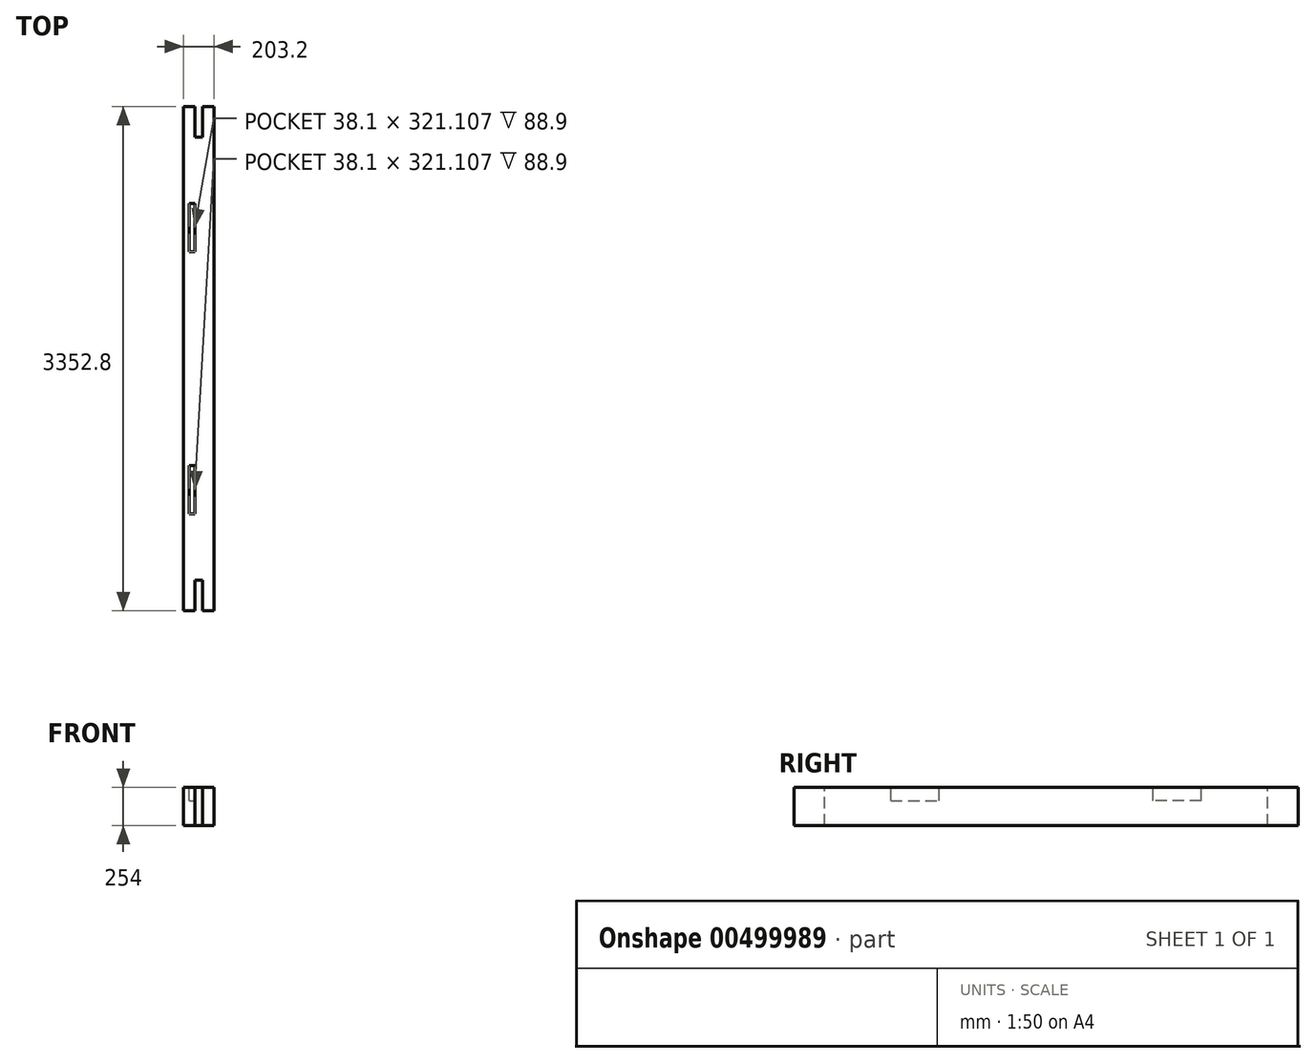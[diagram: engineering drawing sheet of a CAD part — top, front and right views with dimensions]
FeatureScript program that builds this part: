
annotation { "Feature Type Name" : "Feature", "Feature Type Description" : "" }
export const myFeature = defineFeature(function(context is Context, id is Id, definition is map)
    precondition{}
    {
        {
            var Q0;
            Q0=qCreatedBy(makeId("Top.planeOp"),FACE);
            var sketch = newSketch(context, id + "F0", { "sketchPlane" : qUnion([Q0])});
            skLineSegment(sketch, "E0.bottom", {"start": v(-101.6, 1676.4) * mm, "end": v(101.6, 1676.4) * mm});
            skLineSegment(sketch, "E0.top", {"start": v(-101.6, -1676.4) * mm, "end": v(101.6, -1676.4) * mm});
            skLineSegment(sketch, "E0.left", {"start": v(-101.6, 1676.4) * mm, "end": v(-101.6, -1676.4) * mm});
            skLineSegment(sketch, "E0.right", {"start": v(101.6, 1676.4) * mm, "end": v(101.6, -1676.4) * mm});
            skPoint(sketch, "E0.middle", {"position": v(0, 0) * mm});
            skLineSegment(sketch, "E1.bottom", {"start": v(-25.4, -1676.4) * mm, "end": v(25.4, -1676.4) * mm});
            skLineSegment(sketch, "E1.top", {"start": v(-25.4, -1473.2) * mm, "end": v(25.4, -1473.2) * mm});
            skLineSegment(sketch, "E1.left", {"start": v(-25.4, -1676.4) * mm, "end": v(-25.4, -1473.2) * mm});
            skLineSegment(sketch, "E1.right", {"start": v(25.4, -1676.4) * mm, "end": v(25.4, -1473.2) * mm});
            skLineSegment(sketch, "E2.bottom", {"start": v(-63.5, -1032.3) * mm, "end": v(-25.4, -1032.3) * mm});
            skLineSegment(sketch, "E2.top", {"start": v(-63.5, -711.2) * mm, "end": v(-25.4, -711.2) * mm});
            skLineSegment(sketch, "E2.left", {"start": v(-63.5, -1032.3) * mm, "end": v(-63.5, -711.2) * mm});
            skLineSegment(sketch, "E2.right", {"start": v(-25.4, -1032.3) * mm, "end": v(-25.4, -711.2) * mm});
            skLineSegment(sketch, "E3.bottom", {"start": v(-25.4, 1676.4) * mm, "end": v(25.4, 1676.4) * mm});
            skLineSegment(sketch, "E3.top", {"start": v(-25.4, 1473.2) * mm, "end": v(25.4, 1473.2) * mm});
            skLineSegment(sketch, "E3.left", {"start": v(-25.4, 1676.4) * mm, "end": v(-25.4, 1473.2) * mm});
            skLineSegment(sketch, "E3.right", {"start": v(25.4, 1676.4) * mm, "end": v(25.4, 1473.2) * mm});
            skLineSegment(sketch, "E4.bottom", {"start": v(-63.5, 1032.3) * mm, "end": v(-25.4, 1032.3) * mm});
            skLineSegment(sketch, "E4.top", {"start": v(-63.5, 711.2) * mm, "end": v(-25.4, 711.2) * mm});
            skLineSegment(sketch, "E4.left", {"start": v(-63.5, 1032.3) * mm, "end": v(-63.5, 711.2) * mm});
            skLineSegment(sketch, "E4.right", {"start": v(-25.4, 1032.3) * mm, "end": v(-25.4, 711.2) * mm});
            skSolve(sketch);
        }
        {
            var Q0;
            {var subQ3=sQuery(id+"F0.wireOp",EDGE,"E0.left");Q0=makeQuery(id+"F0.imprint","IMPRINT",FACE,{"disambiguationData":[TD([[makeQuery(id+"F0.imprint","IMPRINT",EDGE,{"derivedFrom":subQ3}),1.0]])]});}
            var Q1;
            Q1=makeQuery(id+"F0.imprint","IMPRINT",FACE,{"disambiguationData":[TD([[makeQuery(id+"F0.imprint","IMPRINT",EDGE,{"derivedFrom":sQuery(id+"F0.wireOp",EDGE,"E3.bottom")}),-1.0]])]});
            var Q2;
            Q2=makeQuery(id+"F0.imprint","IMPRINT",FACE,{"disambiguationData":[TD([[makeQuery(id+"F0.imprint","IMPRINT",EDGE,{"derivedFrom":sQuery(id+"F0.wireOp",EDGE,"E4.bottom")}),-1.0]])]});
            var Q3;
            Q3=makeQuery(id+"F0.imprint","IMPRINT",FACE,{"disambiguationData":[TD([[makeQuery(id+"F0.imprint","IMPRINT",EDGE,{"derivedFrom":sQuery(id+"F0.wireOp",EDGE,"E2.bottom")}),1.0]])]});
            var Q4;
            Q4=makeQuery(id+"F0.imprint","IMPRINT",FACE,{"disambiguationData":[TD([[makeQuery(id+"F0.imprint","IMPRINT",EDGE,{"derivedFrom":sQuery(id+"F0.wireOp",EDGE,"E1.bottom")}),1.0]])]});
            extrude(context, id + "F1", {"entities" : qUnion([Q0, Q1, Q2, Q3, Q4]), "oppositeDirection" : true, "depth" : 254 * mm});
        }
        {
            var Q0;
            Q0=makeQuery(id+"F0.imprint","IMPRINT",FACE,{"disambiguationData":[TD([[makeQuery(id+"F0.imprint","IMPRINT",EDGE,{"derivedFrom":sQuery(id+"F0.wireOp",EDGE,"E1.bottom")}),1.0]])]});
            var Q1;
            Q1=makeQuery(id+"F0.imprint","IMPRINT",FACE,{"disambiguationData":[TD([[makeQuery(id+"F0.imprint","IMPRINT",EDGE,{"derivedFrom":sQuery(id+"F0.wireOp",EDGE,"E2.bottom")}),1.0]])]});
            var Q2;
            Q2=makeQuery(id+"F0.imprint","IMPRINT",FACE,{"disambiguationData":[TD([[makeQuery(id+"F0.imprint","IMPRINT",EDGE,{"derivedFrom":sQuery(id+"F0.wireOp",EDGE,"E4.bottom")}),-1.0]])]});
            var Q3;
            Q3=makeQuery(id+"F0.imprint","IMPRINT",FACE,{"disambiguationData":[TD([[makeQuery(id+"F0.imprint","IMPRINT",EDGE,{"derivedFrom":sQuery(id+"F0.wireOp",EDGE,"E3.bottom")}),-1.0]])]});
            extrude(context, id + "F2", {"entities" : qUnion([Q0, Q1, Q2, Q3]), "operationType" : NewBodyOperationType.REMOVE, "oppositeDirection" : true, "depth" : 88.9 * mm});
        }
    });
